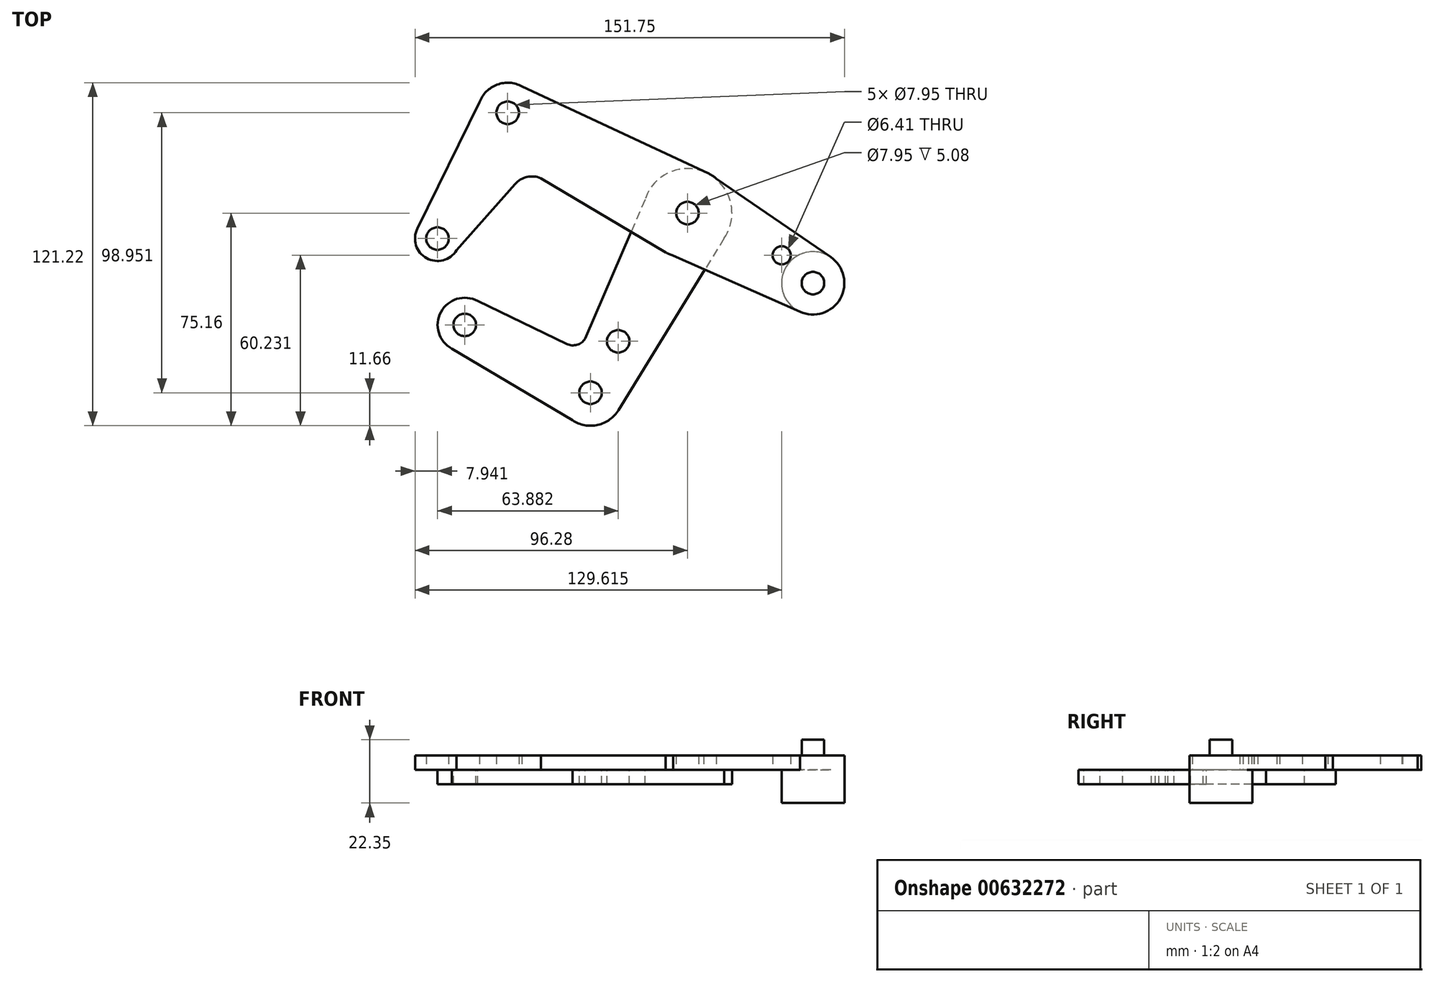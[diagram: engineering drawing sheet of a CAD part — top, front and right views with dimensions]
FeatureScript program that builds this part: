
annotation { "Feature Type Name" : "Feature", "Feature Type Description" : "" }
export const myFeature = defineFeature(function(context is Context, id is Id, definition is map)
    precondition{}
    {
        {
            var Q0;
            Q0=qCreatedBy(makeId("Top.planeOp"),FACE);
            var sketch = newSketch(context, id + "F0", { "sketchPlane" : qUnion([Q0])});
            skCircle(sketch, "E0", {"center": v(0, 0) * mm, "radius": 15.88 * mm});
            skLineSegment(sketch, "E1", {"start": v(0, 0) * mm, "end": v(-54.27, 30.28) * mm});
            skLineSegment(sketch, "E2", {"start": v(0, 0) * mm, "end": v(34.66, -19.34) * mm});
            skCircle(sketch, "E3", {"center": v(0, 0) * mm, "radius": 3.98 * mm});
            skCircle(sketch, "E4", {"center": v(-63.54, 35.45) * mm, "radius": 10.61 * mm});
            skCircle(sketch, "E5", {"center": v(-88.34, -9) * mm, "radius": 7.94 * mm});
            skCircle(sketch, "E6", {"center": v(-63.54, 35.45) * mm, "radius": 3.98 * mm});
            skCircle(sketch, "E7", {"center": v(44.36, -24.75) * mm, "radius": 11.11 * mm});
            skCircle(sketch, "E8", {"center": v(33.33, -14.93) * mm, "radius": 3.2 * mm});
            skCircle(sketch, "E9", {"center": v(-88.34, -9) * mm, "radius": 3.98 * mm});
            skLineSegment(sketch, "E10.trimOffspring", {"start": v(-68.7, 26.18) * mm, "end": v(-84.47, -2.07) * mm});
            skLineSegment(sketch, "E11", {"start": v(-68.7, 26.18) * mm, "end": v(-63.54, 35.45) * mm});
            skLineSegment(sketch, "E12", {"start": v(-63.54, 35.45) * mm, "end": v(-58.46, 44.77) * mm});
            skLineSegment(sketch, "E13", {"start": v(-58.46, 44.77) * mm, "end": v(7.68, 13.9) * mm});
            skLineSegment(sketch, "E14", {"start": v(-81.6, -13.2) * mm, "end": v(-60.92, 10.27) * mm});
            skArc(sketch, "E15", {"start": v(-51.78, 12.3) * mm, "mid": v(-56.68, 12.77) * mm, "end": v(-60.92, 10.27) * mm});
            skLineSegment(sketch, "E16", {"start": v(-51.78, 12.3) * mm, "end": v(-7.74, -13.87) * mm});
            skLineSegment(sketch, "E17", {"start": v(-72.55, 41.06) * mm, "end": v(-95.46, -5.5) * mm});
            skLineSegment(sketch, "E18", {"start": v(39.73, -34.85) * mm, "end": v(-7.74, -13.87) * mm});
            skLineSegment(sketch, "E19", {"start": v(7.68, 13.9) * mm, "end": v(50.65, -15.59) * mm});
            skSolve(sketch);
        }
        {
            var Q0;
            Q0=qCreatedBy(makeId("Top.planeOp"),FACE);
            var sketch = newSketch(context, id + "F1", { "sketchPlane" : qUnion([Q0])});
            skCircle(sketch, "E20", {"center": v(0, 0) * mm, "radius": 15.73 * mm});
            skCircle(sketch, "E21", {"center": v(-34.26, -63.5) * mm, "radius": 11.66 * mm});
            skCircle(sketch, "E22", {"center": v(-34.26, -63.5) * mm, "radius": 3.98 * mm});
            skCircle(sketch, "E23", {"center": v(-24.46, -45.33) * mm, "radius": 3.98 * mm});
            skCircle(sketch, "E24", {"center": v(-78.71, -39.52) * mm, "radius": 9.58 * mm});
            skCircle(sketch, "E25", {"center": v(-78.71, -39.52) * mm, "radius": 3.98 * mm});
            skLineSegment(sketch, "E26", {"start": v(-83.26, -47.95) * mm, "end": v(-39.8, -73.76) * mm});
            skArc(sketch, "E27", {"start": v(-42.67, -46.24) * mm, "mid": v(-39.06, -46.56) * mm, "end": v(-36.16, -44.38) * mm});
            skLineSegment(sketch, "E28", {"start": v(-42.67, -46.24) * mm, "end": v(-74.16, -31.08) * mm});
            skLineSegment(sketch, "E29", {"start": v(-13.74, 7.65) * mm, "end": v(-36.16, -44.38) * mm});
            skLineSegment(sketch, "E30", {"start": v(13.78, -7.58) * mm, "end": v(-24.33, -69.6) * mm});
            skSolve(sketch);
        }
        {
            var Q0;
            Q0 = qSketchRegion(id + "F0", true);
            extrude(context, id + "F2", {"entities" : qUnion([Q0]), "depth" : 5.08 * mm, "offsetDistance" : 25.4 * mm});
        }
        {
            var Q0;
            Q0 = qSketchRegion(id + "F1", true);
            extrude(context, id + "F3", {"entities" : qUnion([Q0]), "operationType" : NewBodyOperationType.ADD, "oppositeDirection" : true, "depth" : 5.08 * mm, "offsetDistance" : 25.4 * mm});
        }
        {
            var Q0;
            {var subQ0=sQuery(id+"F0.wireOp",EDGE,"E7");var subQ1=makeQuery(id+"F0.imprint","INTERSECT",VERTEX,{"derivedFrom":[sQuery(id+"F0.wireOp",EDGE,"E2"),subQ0]});Q0=makeQuery(id+"F0.imprint","IMPRINT",FACE,{"disambiguationData":[TD([[makeQuery(id+"F0.imprint","IMPRINT",EDGE,{"disambiguationData":[TD([[subQ1,1.0]])],"derivedFrom":subQ0}),1.0]])]});}
            extrude(context, id + "F4", {"entities" : qUnion([Q0]), "operationType" : NewBodyOperationType.ADD, "oppositeDirection" : true, "depth" : 11.68 * mm, "offsetDistance" : 25.4 * mm});
        }
        {
            var Q0;
            Q0=makeQuery(id+"F2.opExtrude","CAP_FACE",FACE,{"disambiguationData":[OSD([sQuery(id+"F0.wireOp",EDGE,"E0"),sQuery(id+"F0.wireOp",EDGE,"E3"),sQuery(id+"F0.wireOp",EDGE,"E4"),sQuery(id+"F0.wireOp",EDGE,"E5"),sQuery(id+"F0.wireOp",EDGE,"E6"),sQuery(id+"F0.wireOp",EDGE,"E7"),sQuery(id+"F0.wireOp",EDGE,"E8"),sQuery(id+"F0.wireOp",EDGE,"E9"),sQuery(id+"F0.wireOp",EDGE,"E13"),sQuery(id+"F0.wireOp",EDGE,"E14"),sQuery(id+"F0.wireOp",EDGE,"E15"),sQuery(id+"F0.wireOp",EDGE,"E16"),sQuery(id+"F0.wireOp",EDGE,"E17"),sQuery(id+"F0.wireOp",EDGE,"E18"),sQuery(id+"F0.wireOp",EDGE,"E19")])],"isStart":false});
            var sketch = newSketch(context, id + "F5", { "sketchPlane" : qUnion([Q0])});
            skCircle(sketch, "E31", {"center": v(44.36, -24.75) * mm, "radius": 3.98 * mm});
            skSolve(sketch);
        }
        {
            var Q0;
            Q0=makeQuery(id+"F5.imprint","IMPRINT",FACE,{"disambiguationData":[TD([[makeQuery(id+"F5.imprint","IMPRINT",EDGE,{"derivedFrom":sQuery(id+"F5.wireOp",EDGE,"E31")}),1.0]])]});
            extrude(context, id + "F6", {"entities" : qUnion([Q0]), "operationType" : NewBodyOperationType.ADD, "depth" : 5.6 * mm, "offsetDistance" : 25.4 * mm});
        }
    });
